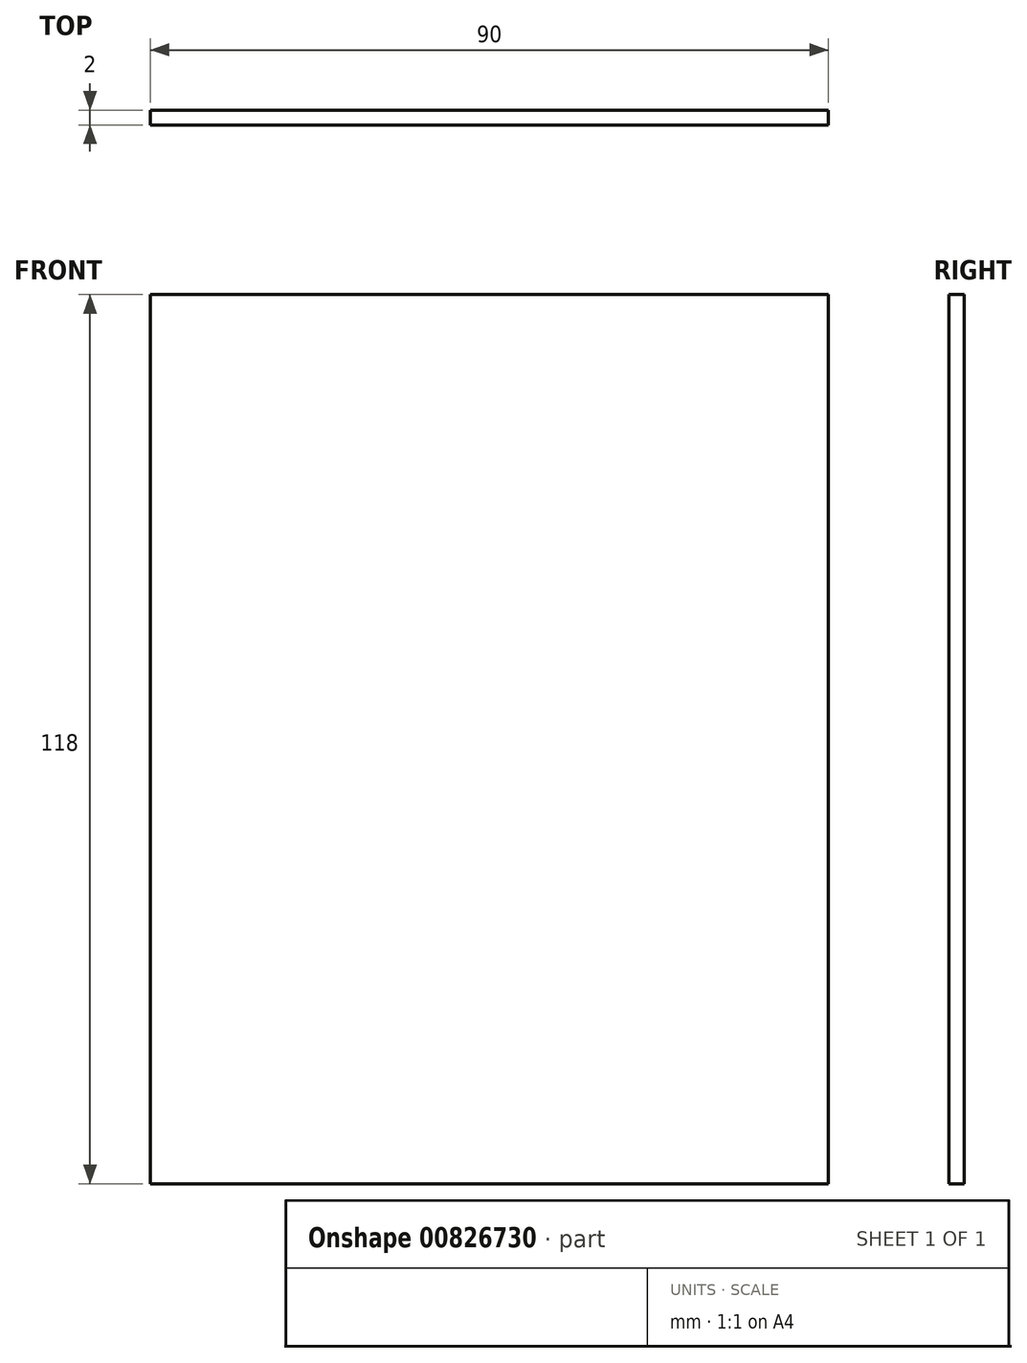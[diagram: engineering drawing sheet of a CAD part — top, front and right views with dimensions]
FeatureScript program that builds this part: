
annotation { "Feature Type Name" : "Feature", "Feature Type Description" : "" }
export const myFeature = defineFeature(function(context is Context, id is Id, definition is map)
    precondition{}
    {
        {
            var Q0;
            Q0=qCreatedBy(makeId("Top.planeOp"),FACE);
            var sketch = newSketch(context, id + "F0", { "sketchPlane" : qUnion([Q0])});
            skLineSegment(sketch, "E0.bottom", {"start": v(45, -1) * mm, "end": v(-45, -1) * mm});
            skLineSegment(sketch, "E0.top", {"start": v(45, 1) * mm, "end": v(-45, 1) * mm});
            skLineSegment(sketch, "E0.left", {"start": v(45, -1) * mm, "end": v(45, 1) * mm});
            skLineSegment(sketch, "E0.right", {"start": v(-45, -1) * mm, "end": v(-45, 1) * mm});
            skPoint(sketch, "E0.middle", {"position": v(0, 0) * mm});
            skSolve(sketch);
        }
        {
            var Q0;
            Q0=makeQuery(id+"F0.imprint","IMPRINT",FACE,{"disambiguationData":[TD([[makeQuery(id+"F0.imprint","IMPRINT",EDGE,{"derivedFrom":sQuery(id+"F0.wireOp",EDGE,"E0.bottom")}),-1.0]])]});
            extrude(context, id + "F1", {"entities" : qUnion([Q0]), "depth" : 118 * mm, "offsetDistance" : 25 * mm});
        }
    });
